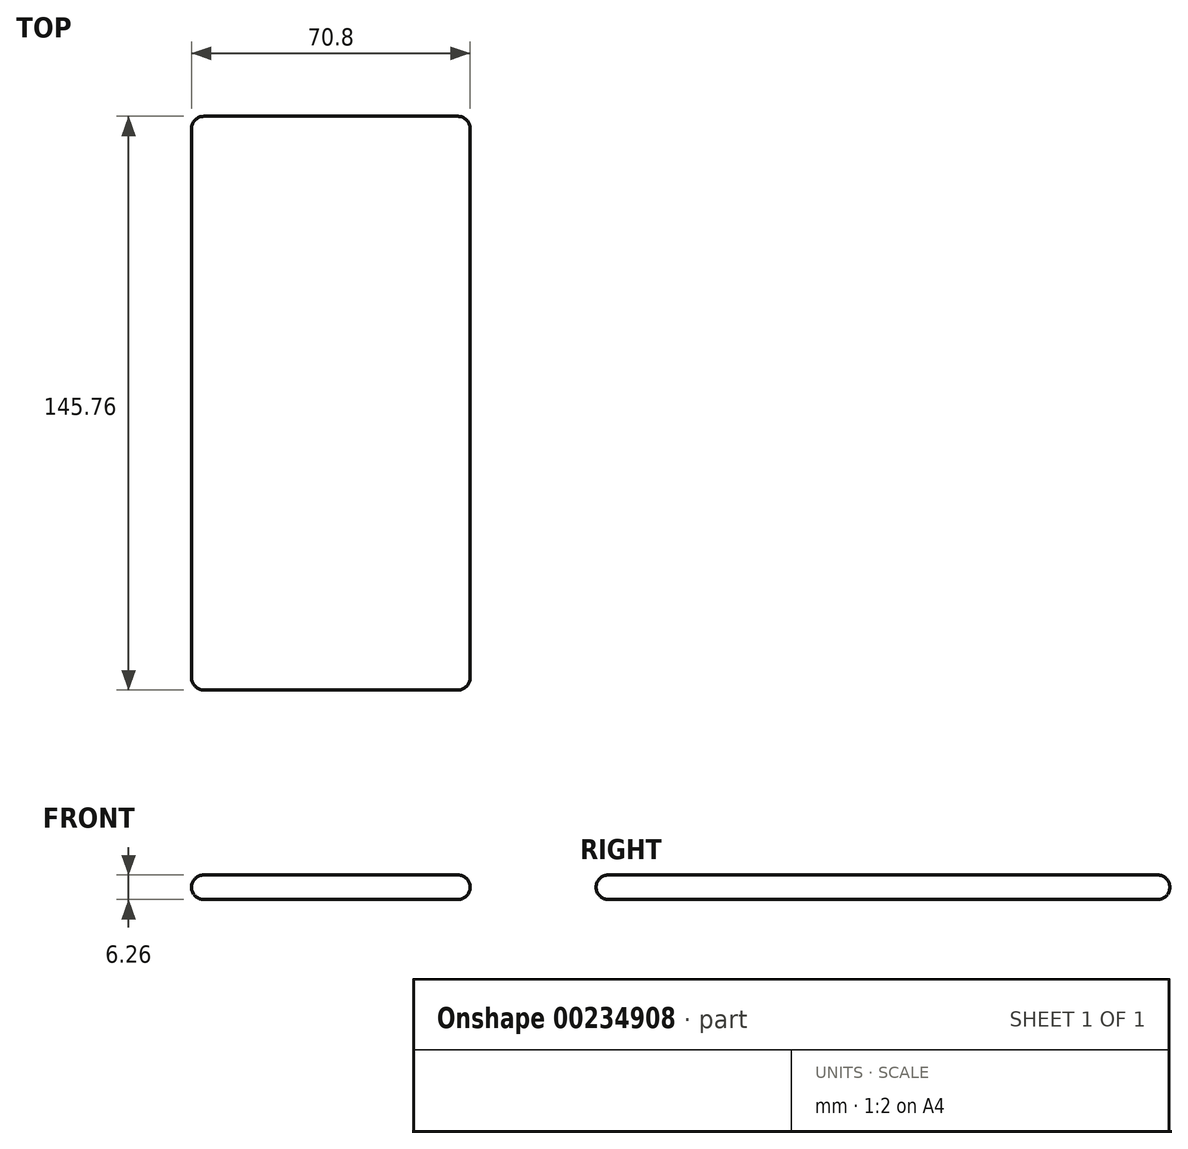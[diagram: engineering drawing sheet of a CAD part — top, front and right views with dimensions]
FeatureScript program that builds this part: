
annotation { "Feature Type Name" : "Feature", "Feature Type Description" : "" }
export const myFeature = defineFeature(function(context is Context, id is Id, definition is map)
    precondition{}
    {
        {
            var Q0;
            Q0=qCreatedBy(makeId("Top.planeOp"),FACE);
            var sketch = newSketch(context, id + "F0", { "sketchPlane" : qUnion([Q0])});
            skLineSegment(sketch, "E0.bottom", {"start": v(35.4, 72.88) * mm, "end": v(-35.4, 72.88) * mm});
            skLineSegment(sketch, "E0.top", {"start": v(35.4, -72.88) * mm, "end": v(-35.4, -72.88) * mm});
            skLineSegment(sketch, "E0.left", {"start": v(35.4, 72.88) * mm, "end": v(35.4, -72.88) * mm});
            skLineSegment(sketch, "E0.right", {"start": v(-35.4, 72.88) * mm, "end": v(-35.4, -72.88) * mm});
            skPoint(sketch, "E0.middle", {"position": v(0, 0) * mm});
            skLineSegment(sketch, "E1.0", {"start": v(-34.9, 69.25) * mm, "end": v(-34.9, -69.25) * mm});
            skLineSegment(sketch, "E1.1", {"start": v(31.77, 72.38) * mm, "end": v(-31.77, 72.38) * mm});
            skLineSegment(sketch, "E1.2", {"start": v(34.9, 69.25) * mm, "end": v(34.9, -69.25) * mm});
            skLineSegment(sketch, "E1.3", {"start": v(31.77, -72.38) * mm, "end": v(-31.77, -72.38) * mm});
            skPoint(sketch, "E2.visualSharp", {"position": v(-34.9, -72.38) * mm});
            skArc(sketch, "E2.filletArc", {"start": v(-34.9, -69.25) * mm, "mid": v(-33.98, -71.46) * mm, "end": v(-31.77, -72.38) * mm});
            skPoint(sketch, "E3.visualSharp", {"position": v(34.9, -72.38) * mm});
            skArc(sketch, "E3.filletArc", {"start": v(31.77, -72.38) * mm, "mid": v(33.98, -71.46) * mm, "end": v(34.9, -69.25) * mm});
            skPoint(sketch, "E4.visualSharp", {"position": v(-34.9, 72.38) * mm});
            skArc(sketch, "E4.filletArc", {"start": v(-31.77, 72.38) * mm, "mid": v(-33.98, 71.46) * mm, "end": v(-34.9, 69.25) * mm});
            skPoint(sketch, "E5.visualSharp", {"position": v(34.9, 72.38) * mm});
            skArc(sketch, "E5.filletArc", {"start": v(34.9, 69.25) * mm, "mid": v(33.98, 71.46) * mm, "end": v(31.77, 72.38) * mm});
            skSolve(sketch);
        }
        {
            var Q0;
            Q0=makeQuery(id+"F0.imprint","IMPRINT",FACE,{"disambiguationData":[TD([[makeQuery(id+"F0.imprint","IMPRINT",EDGE,{"derivedFrom":sQuery(id+"F0.wireOp",EDGE,"E0.bottom")}),1.0]])]});
            var Q1;
            Q1=makeQuery(id+"F0.imprint","IMPRINT",FACE,{"disambiguationData":[TD([[makeQuery(id+"F0.imprint","IMPRINT",EDGE,{"derivedFrom":sQuery(id+"F0.wireOp",EDGE,"E1.0")}),1.0]])]});
            extrude(context, id + "F1", {"entities" : qUnion([Q0, Q1]), "oppositeDirection" : true, "depth" : 6.26 * mm});
        }
        {
            var Q0;
            Q0=makeQuery(id+"F1.opExtrude","CAP_FACE",FACE,{"disambiguationData":[OSD([sQuery(id+"F0.wireOp",EDGE,"E0.bottom"),sQuery(id+"F0.wireOp",EDGE,"E0.top"),sQuery(id+"F0.wireOp",EDGE,"E0.left"),sQuery(id+"F0.wireOp",EDGE,"E0.right")])],"isStart":true});
            var Q1;
            Q1=makeQuery(id+"F1.opExtrude","CAP_FACE",FACE,{"disambiguationData":[OSD([sQuery(id+"F0.wireOp",EDGE,"E0.bottom"),sQuery(id+"F0.wireOp",EDGE,"E0.top"),sQuery(id+"F0.wireOp",EDGE,"E0.left"),sQuery(id+"F0.wireOp",EDGE,"E0.right")])],"isStart":false});
            var Q2;
            Q2=makeQuery(id+"F1.opExtrude","SWEPT_EDGE",EDGE,{"disambiguationData":[OSD([sQuery(id+"F0.wireOp",EDGE,"E0.top"),sQuery(id+"F0.wireOp",EDGE,"E0.left")])]});
            var Q3;
            Q3=makeQuery(id+"F1.opExtrude","SWEPT_EDGE",EDGE,{"disambiguationData":[OSD([sQuery(id+"F0.wireOp",EDGE,"E0.top"),sQuery(id+"F0.wireOp",EDGE,"E0.right")])]});
            var Q4;
            Q4=makeQuery(id+"F1.opExtrude","SWEPT_FACE",FACE,{"disambiguationData":[OSD([sQuery(id+"F0.wireOp",EDGE,"E0.right")])]});
            var Q5;
            Q5=makeQuery(id+"F1.opExtrude","SWEPT_EDGE",EDGE,{"disambiguationData":[OSD([sQuery(id+"F0.wireOp",EDGE,"E0.bottom"),sQuery(id+"F0.wireOp",EDGE,"E0.left")])]});
            fillet(context, id + "F2", {"entities" : qUnion([Q0, Q1, Q2, Q3, Q4, Q5]), "radius" : (6.26 / 2) * mm, "tangentPropagation" : true, "allowEdgeOverflow" : false});
        }
    });
